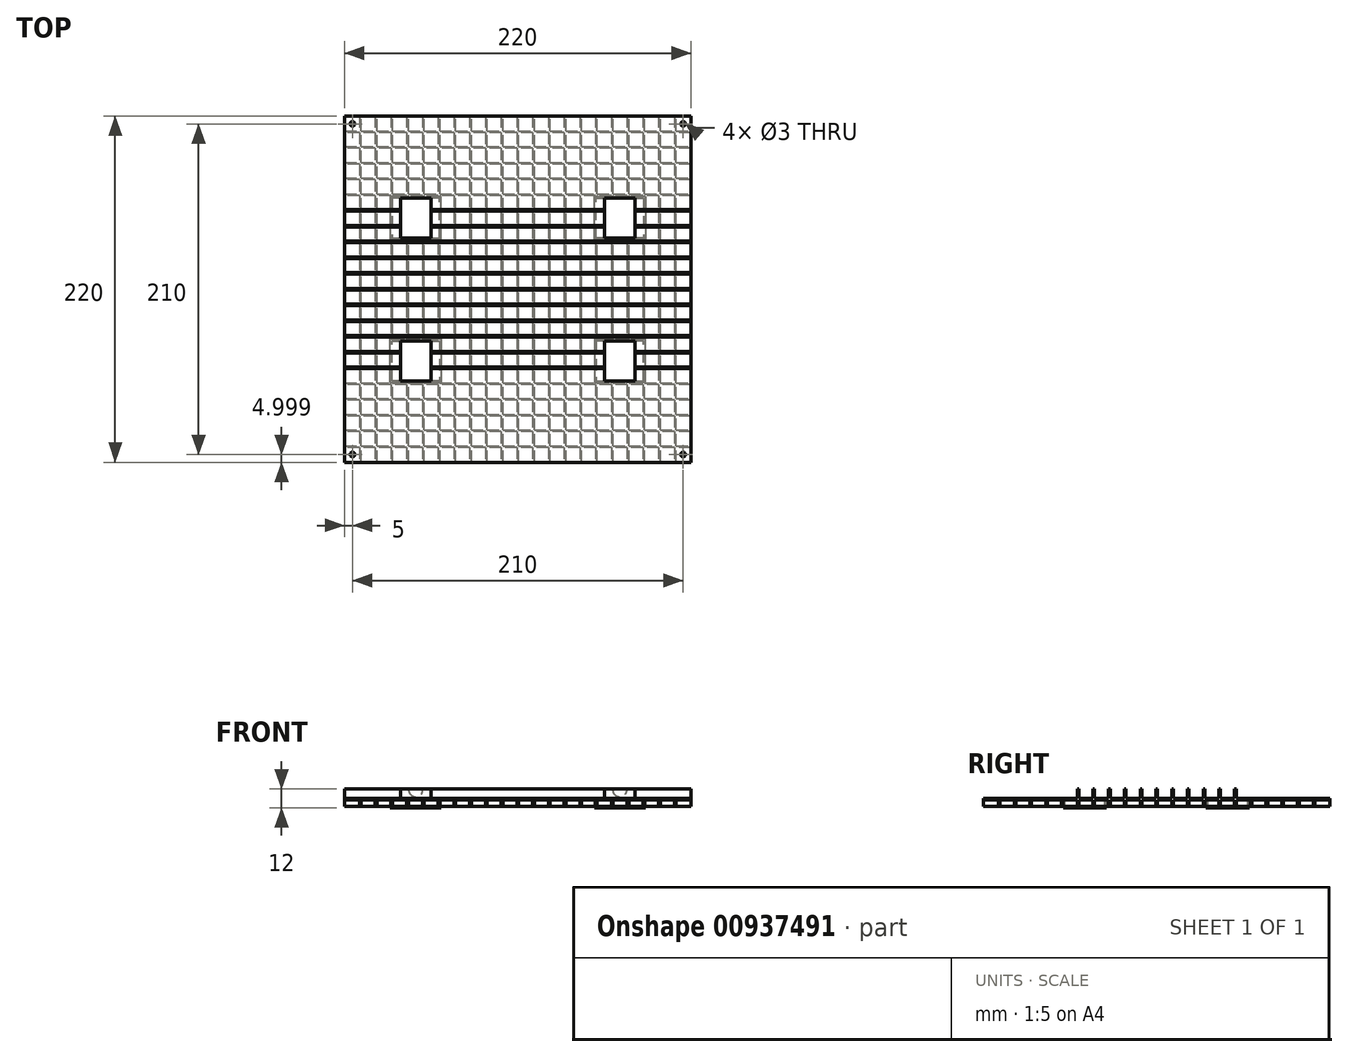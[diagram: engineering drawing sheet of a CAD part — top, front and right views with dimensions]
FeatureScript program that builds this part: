
annotation { "Feature Type Name" : "Feature", "Feature Type Description" : "" }
export const myFeature = defineFeature(function(context is Context, id is Id, definition is map)
    precondition{}
    {
        {
            var Q0;
            Q0=qCreatedBy(makeId("Top.planeOp"),FACE);
            var sketch = newSketch(context, id + "F0", { "sketchPlane" : qUnion([Q0])});
            skPoint(sketch, "E0", {"position": v(-105, 105.2) * mm});
            skPoint(sketch, "E1", {"position": v(105, 105.2) * mm});
            skPoint(sketch, "E2", {"position": v(105, -104.8) * mm});
            skPoint(sketch, "E3", {"position": v(-105, -104.8) * mm});
            skLineSegment(sketch, "E4.bottom", {"start": v(-110, 110.2) * mm, "end": v(110, 110.2) * mm});
            skLineSegment(sketch, "E4.top", {"start": v(-110, -109.8) * mm, "end": v(110, -109.8) * mm});
            skLineSegment(sketch, "E4.left", {"start": v(-110, 110.2) * mm, "end": v(-110, -109.8) * mm});
            skLineSegment(sketch, "E4.right", {"start": v(110, 110.2) * mm, "end": v(110, -109.8) * mm});
            skLineSegment(sketch, "E5", {"start": v(-105, 105.2) * mm, "end": v(-110, 105.2) * mm, "construction": true});
            skLineSegment(sketch, "E6", {"start": v(-105, 105.2) * mm, "end": v(-105, 110.2) * mm, "construction": true});
            skLineSegment(sketch, "E7", {"start": v(105, 105.2) * mm, "end": v(110, 105.2) * mm, "construction": true});
            skLineSegment(sketch, "E8", {"start": v(105, 105.2) * mm, "end": v(105, 110.2) * mm, "construction": true});
            skLineSegment(sketch, "E9", {"start": v(105, -104.8) * mm, "end": v(110, -104.8) * mm, "construction": true});
            skLineSegment(sketch, "E10", {"start": v(105, -104.8) * mm, "end": v(105, -109.8) * mm, "construction": true});
            skLineSegment(sketch, "E11", {"start": v(-105, -104.8) * mm, "end": v(-105, -109.8) * mm, "construction": true});
            skLineSegment(sketch, "E12", {"start": v(-105, -104.8) * mm, "end": v(-110, -104.8) * mm, "construction": true});
            skCircle(sketch, "E13", {"center": v(-105, 105.2) * mm, "radius": 1.5 * mm});
            skCircle(sketch, "E14", {"center": v(105, 105.2) * mm, "radius": 1.5 * mm});
            skCircle(sketch, "E15", {"center": v(105, -104.8) * mm, "radius": 1.5 * mm});
            skCircle(sketch, "E16", {"center": v(-105, -104.8) * mm, "radius": 1.5 * mm});
            skSolve(sketch);
        }
        {
            var Q0;
            Q0 = qSketchRegion(id + "F0", true);
            extrude(context, id + "F1", {"entities" : qUnion([Q0]), "oppositeDirection" : true, "depth" : 1 * mm, "offsetDistance" : 25 * mm});
        }
        {
            var Q0;
            Q0=makeQuery(id+"F1.opExtrude","CAP_FACE",FACE,{"disambiguationData":[OSD([sQuery(id+"F0.wireOp",EDGE,"E4.bottom"),sQuery(id+"F0.wireOp",EDGE,"E4.top"),sQuery(id+"F0.wireOp",EDGE,"E4.left"),sQuery(id+"F0.wireOp",EDGE,"E4.right"),sQuery(id+"F0.wireOp",EDGE,"b305908e-d21f-4fcc-82a1-d083eb46f08c.bottom"),sQuery(id+"F0.wireOp",EDGE,"b305908e-d21f-4fcc-82a1-d083eb46f08c.top"),sQuery(id+"F0.wireOp",EDGE,"b305908e-d21f-4fcc-82a1-d083eb46f08c.left"),sQuery(id+"F0.wireOp",EDGE,"b305908e-d21f-4fcc-82a1-d083eb46f08c.right"),sQuery(id+"F0.wireOp",EDGE,"ffc58e78-ab67-4520-8160-0caf265e7499.bottom"),sQuery(id+"F0.wireOp",EDGE,"ffc58e78-ab67-4520-8160-0caf265e7499.top"),sQuery(id+"F0.wireOp",EDGE,"ffc58e78-ab67-4520-8160-0caf265e7499.left"),sQuery(id+"F0.wireOp",EDGE,"ffc58e78-ab67-4520-8160-0caf265e7499.right"),sQuery(id+"F0.wireOp",EDGE,"050fb597-32a5-4862-9c33-4c7541ed5447.bottom"),sQuery(id+"F0.wireOp",EDGE,"050fb597-32a5-4862-9c33-4c7541ed5447.top"),sQuery(id+"F0.wireOp",EDGE,"050fb597-32a5-4862-9c33-4c7541ed5447.left"),sQuery(id+"F0.wireOp",EDGE,"050fb597-32a5-4862-9c33-4c7541ed5447.right"),sQuery(id+"F0.wireOp",EDGE,"796d922f-7def-4038-baac-653a5c7ec2cd.bottom"),sQuery(id+"F0.wireOp",EDGE,"796d922f-7def-4038-baac-653a5c7ec2cd.top"),sQuery(id+"F0.wireOp",EDGE,"796d922f-7def-4038-baac-653a5c7ec2cd.left"),sQuery(id+"F0.wireOp",EDGE,"796d922f-7def-4038-baac-653a5c7ec2cd.right"),sQuery(id+"F0.wireOp",EDGE,"E13"),sQuery(id+"F0.wireOp",EDGE,"E14"),sQuery(id+"F0.wireOp",EDGE,"E15"),sQuery(id+"F0.wireOp",EDGE,"E16")])],"isStart":false});
            var sketch = newSketch(context, id + "F2", { "sketchPlane" : qUnion([Q0])});
            skPoint(sketch, "E17.0", {"position": v(110, -110) * mm});
            skPoint(sketch, "E17.1", {"position": v(-110, -110) * mm});
            skPoint(sketch, "E17.2", {"position": v(110, 110) * mm});
            skPoint(sketch, "E17.3", {"position": v(-110, 110) * mm});
            skLineSegment(sketch, "E17.4", {"start": v(49.6, -32.6) * mm, "end": v(49.6, -58) * mm});
            skLineSegment(sketch, "E17.5", {"start": v(49.6, -58) * mm, "end": v(80, -58) * mm});
            skLineSegment(sketch, "E17.6", {"start": v(80, -58) * mm, "end": v(80, -32.6) * mm});
            skLineSegment(sketch, "E17.7", {"start": v(80, -32.6) * mm, "end": v(49.6, -32.6) * mm});
            skLineSegment(sketch, "E18", {"start": v(110, 110) * mm, "end": v(110, -110) * mm});
            skLineSegment(sketch, "E19", {"start": v(110, -110) * mm, "end": v(-110, -110) * mm});
            skLineSegment(sketch, "E20", {"start": v(-110, 110) * mm, "end": v(110, 110) * mm});
            skLineSegment(sketch, "E21", {"start": v(74.6, -58) * mm, "end": v(74.6, -32.6) * mm});
            skLineSegment(sketch, "E22", {"start": v(55, -58) * mm, "end": v(55, -32.6) * mm});
            skLineSegment(sketch, "E23.0", {"start": v(81, -31.6) * mm, "end": v(48.6, -31.6) * mm});
            skLineSegment(sketch, "E23.1", {"start": v(81, -59) * mm, "end": v(81, -31.6) * mm});
            skLineSegment(sketch, "E23.2", {"start": v(48.6, -59) * mm, "end": v(81, -59) * mm});
            skLineSegment(sketch, "E23.3", {"start": v(48.6, -31.6) * mm, "end": v(48.6, -59) * mm});
            skLineSegment(sketch, "E24", {"start": v(0, 0) * mm, "end": v(0, -10.79) * mm, "construction": true});
            skLineSegment(sketch, "E25", {"start": v(0, 0) * mm, "end": v(11.86, 0) * mm, "construction": true});
            skLineSegment(sketch, "E26.MirrorCS", {"start": v(-49.6, -58) * mm, "end": v(-80, -58) * mm});
            skLineSegment(sketch, "E27.MirrorCS", {"start": v(-80, -58) * mm, "end": v(-80, -32.6) * mm});
            skLineSegment(sketch, "E28.MirrorCS", {"start": v(-81, -59) * mm, "end": v(-81, -31.6) * mm});
            skLineSegment(sketch, "E29.MirrorCS", {"start": v(-55, -58) * mm, "end": v(-55, -32.6) * mm});
            skLineSegment(sketch, "E30.MirrorCS", {"start": v(-81, -31.6) * mm, "end": v(-48.6, -31.6) * mm});
            skLineSegment(sketch, "E31.MirrorCS", {"start": v(-48.6, -59) * mm, "end": v(-81, -59) * mm});
            skLineSegment(sketch, "E32.MirrorCS", {"start": v(-74.6, -58) * mm, "end": v(-74.6, -32.6) * mm});
            skLineSegment(sketch, "E33.MirrorCS", {"start": v(-80, -32.6) * mm, "end": v(-49.6, -32.6) * mm});
            skLineSegment(sketch, "E34.MirrorCS", {"start": v(-49.6, -32.6) * mm, "end": v(-49.6, -58) * mm});
            skLineSegment(sketch, "E35.MirrorCS", {"start": v(-48.6, -31.6) * mm, "end": v(-48.6, -59) * mm});
            skLineSegment(sketch, "E36.MirrorCS", {"start": v(-55, 58) * mm, "end": v(-55, 32.6) * mm});
            skLineSegment(sketch, "E37.MirrorCS", {"start": v(-80, 58) * mm, "end": v(-80, 32.6) * mm});
            skLineSegment(sketch, "E38.MirrorCS", {"start": v(48.6, 59) * mm, "end": v(81, 59) * mm});
            skLineSegment(sketch, "E39.MirrorCS", {"start": v(74.6, 58) * mm, "end": v(74.6, 32.6) * mm});
            skLineSegment(sketch, "E40.MirrorCS", {"start": v(49.6, 58) * mm, "end": v(80, 58) * mm});
            skLineSegment(sketch, "E41.MirrorCS", {"start": v(-80, 32.6) * mm, "end": v(-49.6, 32.6) * mm});
            skLineSegment(sketch, "E42.MirrorCS", {"start": v(80, 32.6) * mm, "end": v(49.6, 32.6) * mm});
            skLineSegment(sketch, "E43.MirrorCS", {"start": v(-81, 59) * mm, "end": v(-81, 31.6) * mm});
            skLineSegment(sketch, "E44.MirrorCS", {"start": v(49.6, 32.6) * mm, "end": v(49.6, 58) * mm});
            skLineSegment(sketch, "E45.MirrorCS", {"start": v(-48.6, 59) * mm, "end": v(-81, 59) * mm});
            skLineSegment(sketch, "E46.MirrorCS", {"start": v(-48.6, 31.6) * mm, "end": v(-48.6, 59) * mm});
            skLineSegment(sketch, "E47.MirrorCS", {"start": v(81, 31.6) * mm, "end": v(48.6, 31.6) * mm});
            skLineSegment(sketch, "E48.MirrorCS", {"start": v(-49.6, 32.6) * mm, "end": v(-49.6, 58) * mm});
            skLineSegment(sketch, "E49.MirrorCS", {"start": v(-49.6, 58) * mm, "end": v(-80, 58) * mm});
            skLineSegment(sketch, "E50.MirrorCS", {"start": v(81, 59) * mm, "end": v(81, 31.6) * mm});
            skLineSegment(sketch, "E51.MirrorCS", {"start": v(48.6, 31.6) * mm, "end": v(48.6, 59) * mm});
            skLineSegment(sketch, "E52.MirrorCS", {"start": v(55, 58) * mm, "end": v(55, 32.6) * mm});
            skLineSegment(sketch, "E53.MirrorCS", {"start": v(80, 58) * mm, "end": v(80, 32.6) * mm});
            skLineSegment(sketch, "E54.MirrorCS", {"start": v(-74.6, 58) * mm, "end": v(-74.6, 32.6) * mm});
            skLineSegment(sketch, "E55.MirrorCS", {"start": v(-81, 31.6) * mm, "end": v(-48.6, 31.6) * mm});
            skSolve(sketch);
        }
        {
            var Q0;
            Q0=qCreatedBy(makeId("Top.planeOp"),FACE);
            var sketch = newSketch(context, id + "F3", { "sketchPlane" : qUnion([Q0])});
            skLineSegment(sketch, "E56.0", {"start": v(-110, 110.2) * mm, "end": v(110, 110.2) * mm, "construction": true});
            skLineSegment(sketch, "E56.19", {"start": v(-110, -109.8) * mm, "end": v(110, -109.8) * mm, "construction": true});
            skCircle(sketch, "E56.20", {"center": v(-105, -104.8) * mm, "radius": 1.5 * mm, "construction": true});
            skCircle(sketch, "E56.21", {"center": v(105, -104.8) * mm, "radius": 1.5 * mm, "construction": true});
            skCircle(sketch, "E56.22", {"center": v(105, 105.2) * mm, "radius": 1.5 * mm, "construction": true});
            skCircle(sketch, "E56.23", {"center": v(-105, 105.2) * mm, "radius": 1.5 * mm, "construction": true});
            skLineSegment(sketch, "E57", {"start": v(-110, 100.7) * mm, "end": v(110, 100.7) * mm});
            skLineSegment(sketch, "E58", {"start": v(110, 99.7) * mm, "end": v(-110, 99.7) * mm});
            skLineSegment(sketch, "E59.0.1.0", {"start": v(-110, 90.7) * mm, "end": v(110, 90.7) * mm});
            skLineSegment(sketch, "E59.0.1.1", {"start": v(110, 89.7) * mm, "end": v(-110, 89.7) * mm});
            skLineSegment(sketch, "E59.0.2.0", {"start": v(-110, 80.7) * mm, "end": v(110, 80.7) * mm});
            skLineSegment(sketch, "E59.0.2.1", {"start": v(110, 79.7) * mm, "end": v(-110, 79.7) * mm});
            skLineSegment(sketch, "E59.0.3.0", {"start": v(-110, 70.7) * mm, "end": v(110, 70.7) * mm});
            skLineSegment(sketch, "E59.0.3.1", {"start": v(110, 69.7) * mm, "end": v(-110, 69.7) * mm});
            skLineSegment(sketch, "E59.0.4.0", {"start": v(-110, 60.7) * mm, "end": v(110, 60.7) * mm});
            skLineSegment(sketch, "E59.0.4.1", {"start": v(110, 59.7) * mm, "end": v(-110, 59.7) * mm});
            skLineSegment(sketch, "E59.0.5.0", {"start": v(-110, 50.7) * mm, "end": v(110, 50.7) * mm});
            skLineSegment(sketch, "E59.0.5.1", {"start": v(110, 49.7) * mm, "end": v(-110, 49.7) * mm});
            skLineSegment(sketch, "E59.0.6.0", {"start": v(-110, 40.7) * mm, "end": v(110, 40.7) * mm});
            skLineSegment(sketch, "E59.0.6.1", {"start": v(110, 39.7) * mm, "end": v(-110, 39.7) * mm});
            skLineSegment(sketch, "E59.0.7.0", {"start": v(-110, 30.7) * mm, "end": v(110, 30.7) * mm});
            skLineSegment(sketch, "E59.0.7.1", {"start": v(110, 29.7) * mm, "end": v(-110, 29.7) * mm});
            skLineSegment(sketch, "E59.0.8.0", {"start": v(-110, 20.7) * mm, "end": v(110, 20.7) * mm});
            skLineSegment(sketch, "E59.0.8.1", {"start": v(110, 19.7) * mm, "end": v(-110, 19.7) * mm});
            skLineSegment(sketch, "E59.0.9.0", {"start": v(-110, 10.7) * mm, "end": v(110, 10.7) * mm});
            skLineSegment(sketch, "E59.0.9.1", {"start": v(110, 9.7) * mm, "end": v(-110, 9.7) * mm});
            skLineSegment(sketch, "E59.0.10.0", {"start": v(-110, 0.7) * mm, "end": v(110, 0.7) * mm});
            skLineSegment(sketch, "E59.0.10.1", {"start": v(110, -0.3) * mm, "end": v(-110, -0.3) * mm});
            skLineSegment(sketch, "E59.0.11.0", {"start": v(-110, -9.3) * mm, "end": v(110, -9.3) * mm});
            skLineSegment(sketch, "E59.0.11.1", {"start": v(110, -10.3) * mm, "end": v(-110, -10.3) * mm});
            skLineSegment(sketch, "E59.0.12.0", {"start": v(-110, -19.3) * mm, "end": v(110, -19.3) * mm});
            skLineSegment(sketch, "E59.0.12.1", {"start": v(110, -20.3) * mm, "end": v(-110, -20.3) * mm});
            skLineSegment(sketch, "E59.0.13.0", {"start": v(-110, -29.3) * mm, "end": v(110, -29.3) * mm});
            skLineSegment(sketch, "E59.0.13.1", {"start": v(110, -30.3) * mm, "end": v(-110, -30.3) * mm});
            skLineSegment(sketch, "E59.0.14.0", {"start": v(-110, -39.3) * mm, "end": v(110, -39.3) * mm});
            skLineSegment(sketch, "E59.0.14.1", {"start": v(110, -40.3) * mm, "end": v(-110, -40.3) * mm});
            skLineSegment(sketch, "E59.0.15.0", {"start": v(-110, -49.3) * mm, "end": v(110, -49.3) * mm});
            skLineSegment(sketch, "E59.0.15.1", {"start": v(110, -50.3) * mm, "end": v(-110, -50.3) * mm});
            skLineSegment(sketch, "E59.0.16.0", {"start": v(-110, -59.3) * mm, "end": v(110, -59.3) * mm});
            skLineSegment(sketch, "E59.0.16.1", {"start": v(110, -60.3) * mm, "end": v(-110, -60.3) * mm});
            skLineSegment(sketch, "E59.0.17.0", {"start": v(-110, -69.3) * mm, "end": v(110, -69.3) * mm});
            skLineSegment(sketch, "E59.0.17.1", {"start": v(110, -70.3) * mm, "end": v(-110, -70.3) * mm});
            skLineSegment(sketch, "E59.0.18.0", {"start": v(-110, -79.3) * mm, "end": v(110, -79.3) * mm});
            skLineSegment(sketch, "E59.0.18.1", {"start": v(110, -80.3) * mm, "end": v(-110, -80.3) * mm});
            skLineSegment(sketch, "E59.0.19.0", {"start": v(-110, -89.3) * mm, "end": v(110, -89.3) * mm});
            skLineSegment(sketch, "E59.0.19.1", {"start": v(110, -90.3) * mm, "end": v(-110, -90.3) * mm});
            skLineSegment(sketch, "E59.0.20.0", {"start": v(-110, -99.3) * mm, "end": v(110, -99.3) * mm});
            skLineSegment(sketch, "E59.0.20.1", {"start": v(110, -100.3) * mm, "end": v(-110, -100.3) * mm});
            skLineSegment(sketch, "E59.direction1", {"start": v(-110, 99.7) * mm, "end": v(-85, 99.7) * mm, "construction": true});
            skLineSegment(sketch, "E60", {"start": v(-110, 100.7) * mm, "end": v(-110, 99.7) * mm});
            skLineSegment(sketch, "E61", {"start": v(110, -100.3) * mm, "end": v(110, -99.3) * mm});
            skLineSegment(sketch, "E62.trimOffspring", {"start": v(110, 99.7) * mm, "end": v(110, 100.7) * mm});
            skLineSegment(sketch, "E63.trimOffspring", {"start": v(110, 89.7) * mm, "end": v(110, 90.7) * mm});
            skLineSegment(sketch, "E64.trimOffspring", {"start": v(110, 79.7) * mm, "end": v(110, 80.7) * mm});
            skLineSegment(sketch, "E65.trimOffspring", {"start": v(110, 69.7) * mm, "end": v(110, 70.7) * mm});
            skLineSegment(sketch, "E66.trimOffspring", {"start": v(110, 59.7) * mm, "end": v(110, 60.7) * mm});
            skLineSegment(sketch, "E67.trimOffspring", {"start": v(110, 49.7) * mm, "end": v(110, 50.7) * mm});
            skLineSegment(sketch, "E68.trimOffspring", {"start": v(110, 39.7) * mm, "end": v(110, 40.7) * mm});
            skLineSegment(sketch, "E69.trimOffspring", {"start": v(110, 29.7) * mm, "end": v(110, 30.7) * mm});
            skLineSegment(sketch, "E70.trimOffspring", {"start": v(110, 19.7) * mm, "end": v(110, 20.7) * mm});
            skLineSegment(sketch, "E71.trimOffspring", {"start": v(110, 9.7) * mm, "end": v(110, 10.7) * mm});
            skLineSegment(sketch, "E72.trimOffspring", {"start": v(110, -0.3) * mm, "end": v(110, 0.7) * mm});
            skLineSegment(sketch, "E73.trimOffspring", {"start": v(110, -10.3) * mm, "end": v(110, -9.3) * mm});
            skLineSegment(sketch, "E74.trimOffspring", {"start": v(110, -20.3) * mm, "end": v(110, -19.3) * mm});
            skLineSegment(sketch, "E75.trimOffspring", {"start": v(110, -30.3) * mm, "end": v(110, -29.3) * mm});
            skLineSegment(sketch, "E76.trimOffspring", {"start": v(110, -40.3) * mm, "end": v(110, -39.3) * mm});
            skLineSegment(sketch, "E77.trimOffspring", {"start": v(110, -50.3) * mm, "end": v(110, -49.3) * mm});
            skLineSegment(sketch, "E78.trimOffspring", {"start": v(110, -60.3) * mm, "end": v(110, -59.3) * mm});
            skLineSegment(sketch, "E79.trimOffspring", {"start": v(110, -70.3) * mm, "end": v(110, -69.3) * mm});
            skLineSegment(sketch, "E80.trimOffspring", {"start": v(110, -80.3) * mm, "end": v(110, -79.3) * mm});
            skLineSegment(sketch, "E81.trimOffspring", {"start": v(110, -90.3) * mm, "end": v(110, -89.3) * mm});
            skLineSegment(sketch, "E82.trimOffspring", {"start": v(-110, -99.3) * mm, "end": v(-110, -100.3) * mm});
            skLineSegment(sketch, "E83.trimOffspring", {"start": v(-110, -89.3) * mm, "end": v(-110, -90.3) * mm});
            skLineSegment(sketch, "E84.trimOffspring", {"start": v(-110, -79.3) * mm, "end": v(-110, -80.3) * mm});
            skLineSegment(sketch, "E85.trimOffspring", {"start": v(-110, -69.3) * mm, "end": v(-110, -70.3) * mm});
            skLineSegment(sketch, "E86.trimOffspring", {"start": v(-110, -59.3) * mm, "end": v(-110, -60.3) * mm});
            skLineSegment(sketch, "E87.trimOffspring", {"start": v(-110, -49.3) * mm, "end": v(-110, -50.3) * mm});
            skLineSegment(sketch, "E88.trimOffspring", {"start": v(-110, -39.3) * mm, "end": v(-110, -40.3) * mm});
            skLineSegment(sketch, "E89.trimOffspring", {"start": v(-110, -29.3) * mm, "end": v(-110, -30.3) * mm});
            skLineSegment(sketch, "E90.trimOffspring", {"start": v(-110, -19.3) * mm, "end": v(-110, -20.3) * mm});
            skLineSegment(sketch, "E91.trimOffspring", {"start": v(-110, -9.3) * mm, "end": v(-110, -10.3) * mm});
            skLineSegment(sketch, "E92.trimOffspring", {"start": v(-110, 0.7) * mm, "end": v(-110, -0.3) * mm});
            skLineSegment(sketch, "E93.trimOffspring", {"start": v(-110, 10.7) * mm, "end": v(-110, 9.7) * mm});
            skLineSegment(sketch, "E94.trimOffspring", {"start": v(-110, 20.7) * mm, "end": v(-110, 19.7) * mm});
            skLineSegment(sketch, "E95.trimOffspring", {"start": v(-110, 30.7) * mm, "end": v(-110, 29.7) * mm});
            skLineSegment(sketch, "E96.trimOffspring", {"start": v(-110, 40.7) * mm, "end": v(-110, 39.7) * mm});
            skLineSegment(sketch, "E97.trimOffspring", {"start": v(-110, 50.7) * mm, "end": v(-110, 49.7) * mm});
            skLineSegment(sketch, "E98.trimOffspring", {"start": v(-110, 60.7) * mm, "end": v(-110, 59.7) * mm});
            skLineSegment(sketch, "E99.trimOffspring", {"start": v(-110, 70.7) * mm, "end": v(-110, 69.7) * mm});
            skLineSegment(sketch, "E100.trimOffspring", {"start": v(-110, 80.7) * mm, "end": v(-110, 79.7) * mm});
            skLineSegment(sketch, "E101.trimOffspring", {"start": v(-110, 90.7) * mm, "end": v(-110, 89.7) * mm});
            skLineSegment(sketch, "E102.0", {"start": v(70, -29.3) * mm, "end": v(70, -30.3) * mm});
            skLineSegment(sketch, "E102.1", {"start": v(101, -50.3) * mm, "end": v(101, -49.3) * mm});
            skLineSegment(sketch, "E103.0", {"start": v(101, 29.7) * mm, "end": v(101, 30.7) * mm});
            skLineSegment(sketch, "E103.1", {"start": v(70, 29.7) * mm, "end": v(70, 30.7) * mm});
            skLineSegment(sketch, "E103.2", {"start": v(-70, 29.7) * mm, "end": v(-70, 30.7) * mm});
            skLineSegment(sketch, "E103.3", {"start": v(-101, 29.7) * mm, "end": v(-101, 30.7) * mm});
            skLineSegment(sketch, "E103.4", {"start": v(-101, -29.3) * mm, "end": v(-101, -30.3) * mm});
            skLineSegment(sketch, "E103.5", {"start": v(-70, -29.3) * mm, "end": v(-70, -30.3) * mm});
            skLineSegment(sketch, "E104.trimOffspring", {"start": v(101, 49.7) * mm, "end": v(101, 50.7) * mm});
            skLineSegment(sketch, "E105.trimOffspring", {"start": v(101, 39.7) * mm, "end": v(101, 40.7) * mm});
            skLineSegment(sketch, "E106.trimOffspring", {"start": v(70, 39.7) * mm, "end": v(70, 40.7) * mm});
            skLineSegment(sketch, "E107.trimOffspring", {"start": v(70, 49.7) * mm, "end": v(70, 50.7) * mm});
            skLineSegment(sketch, "E108.trimOffspring", {"start": v(-70, 49.7) * mm, "end": v(-70, 50.7) * mm});
            skLineSegment(sketch, "E109.trimOffspring", {"start": v(-70, 39.7) * mm, "end": v(-70, 40.7) * mm});
            skLineSegment(sketch, "E110.trimOffspring", {"start": v(-101, 39.7) * mm, "end": v(-101, 40.7) * mm});
            skLineSegment(sketch, "E111.trimOffspring", {"start": v(-101, 49.7) * mm, "end": v(-101, 50.7) * mm});
            skLineSegment(sketch, "E112.trimOffspring", {"start": v(-101, -39.3) * mm, "end": v(-101, -40.3) * mm});
            skLineSegment(sketch, "E113.trimOffspring", {"start": v(-101, -49.3) * mm, "end": v(-101, -50.3) * mm});
            skLineSegment(sketch, "E114.trimOffspring", {"start": v(-70, -49.3) * mm, "end": v(-70, -50.3) * mm});
            skLineSegment(sketch, "E115.trimOffspring", {"start": v(-70, -39.3) * mm, "end": v(-70, -40.3) * mm});
            skLineSegment(sketch, "E116.trimOffspring", {"start": v(101, -30.3) * mm, "end": v(101, -29.3) * mm});
            skLineSegment(sketch, "E117.trimOffspring", {"start": v(70, -39.3) * mm, "end": v(70, -40.3) * mm});
            skLineSegment(sketch, "E118.trimOffspring", {"start": v(70, -49.3) * mm, "end": v(70, -50.3) * mm});
            skLineSegment(sketch, "E119", {"start": v(101, -39.3) * mm, "end": v(101, -40.3) * mm});
            skPoint(sketch, "E120.0", {"position": v(-110, 110.2) * mm});
            skSolve(sketch);
        }
        {
            var Q0;
            Q0=makeQuery(id+"F3.imprint","IMPRINT",FACE,{"disambiguationData":[TD([[makeQuery(id+"F3.imprint","IMPRINT",EDGE,{"derivedFrom":sQuery(id+"F3.wireOp",EDGE,"E59.0.18.0")}),-1.0]])]});
            var Q1;
            Q1=makeQuery(id+"F3.imprint","IMPRINT",FACE,{"disambiguationData":[TD([[makeQuery(id+"F3.imprint","IMPRINT",EDGE,{"derivedFrom":sQuery(id+"F3.wireOp",EDGE,"E59.0.17.0")}),-1.0]])]});
            var Q2;
            Q2=makeQuery(id+"F3.imprint","IMPRINT",FACE,{"disambiguationData":[TD([[makeQuery(id+"F3.imprint","IMPRINT",EDGE,{"derivedFrom":sQuery(id+"F3.wireOp",EDGE,"E59.0.16.0")}),-1.0]])]});
            var Q3;
            Q3=makeQuery(id+"F3.imprint","IMPRINT",FACE,{"disambiguationData":[TD([[makeQuery(id+"F3.imprint","IMPRINT",EDGE,{"derivedFrom":sQuery(id+"F3.wireOp",EDGE,"E59.0.11.0")}),-1.0]])]});
            var Q4;
            Q4=makeQuery(id+"F3.imprint","IMPRINT",FACE,{"disambiguationData":[TD([[makeQuery(id+"F3.imprint","IMPRINT",EDGE,{"derivedFrom":sQuery(id+"F3.wireOp",EDGE,"E59.0.10.0")}),-1.0]])]});
            var Q5;
            Q5=makeQuery(id+"F3.imprint","IMPRINT",FACE,{"disambiguationData":[TD([[makeQuery(id+"F3.imprint","IMPRINT",EDGE,{"derivedFrom":sQuery(id+"F3.wireOp",EDGE,"E59.0.9.0")}),-1.0]])]});
            var Q6;
            Q6=makeQuery(id+"F3.imprint","IMPRINT",FACE,{"disambiguationData":[TD([[makeQuery(id+"F3.imprint","IMPRINT",EDGE,{"derivedFrom":sQuery(id+"F3.wireOp",EDGE,"E59.0.4.0")}),-1.0]])]});
            var Q7;
            Q7=makeQuery(id+"F3.imprint","IMPRINT",FACE,{"disambiguationData":[TD([[makeQuery(id+"F3.imprint","IMPRINT",EDGE,{"derivedFrom":sQuery(id+"F3.wireOp",EDGE,"E59.0.3.0")}),-1.0]])]});
            var Q8;
            Q8=makeQuery(id+"F3.imprint","IMPRINT",FACE,{"disambiguationData":[TD([[makeQuery(id+"F3.imprint","IMPRINT",EDGE,{"derivedFrom":sQuery(id+"F3.wireOp",EDGE,"E59.0.2.0")}),-1.0]])]});
            var Q9;
            {var subQ1=sQuery(id+"F2.wireOp",EDGE,"E17.4");Q9=makeQuery(id+"F2.imprint","IMPRINT",FACE,{"disambiguationData":[TD([[makeQuery(id+"F2.imprint","IMPRINT",EDGE,{"derivedFrom":subQ1}),-1.0]])]});}
            var Q10;
            Q10=makeQuery(id+"F3.imprint","IMPRINT",FACE,{"disambiguationData":[TD([[makeQuery(id+"F3.imprint","IMPRINT",EDGE,{"derivedFrom":sQuery(id+"F3.wireOp",EDGE,"E57")}),-1.0]])]});
            var Q11;
            Q11=makeQuery(id+"F3.imprint","IMPRINT",FACE,{"disambiguationData":[TD([[makeQuery(id+"F3.imprint","IMPRINT",EDGE,{"derivedFrom":sQuery(id+"F3.wireOp",EDGE,"E59.0.1.0")}),-1.0]])]});
            var Q12;
            {var subQ0=sQuery(id+"F3.wireOp",EDGE,"E97.trimOffspring");Q12=makeQuery(id+"F3.imprint","IMPRINT",FACE,{"disambiguationData":[TD([[makeQuery(id+"F3.imprint","IMPRINT",EDGE,{"derivedFrom":subQ0}),1.0]])]});}
            var Q13;
            {var subQ0=sQuery(id+"F3.wireOp",EDGE,"E107.trimOffspring");Q13=makeQuery(id+"F3.imprint","IMPRINT",FACE,{"disambiguationData":[TD([[makeQuery(id+"F3.imprint","IMPRINT",EDGE,{"derivedFrom":subQ0}),1.0]])]});}
            var Q14;
            {var subQ0=sQuery(id+"F3.wireOp",EDGE,"E106.trimOffspring");Q14=makeQuery(id+"F3.imprint","IMPRINT",FACE,{"disambiguationData":[TD([[makeQuery(id+"F3.imprint","IMPRINT",EDGE,{"derivedFrom":subQ0}),1.0]])]});}
            var Q15;
            {var subQ0=sQuery(id+"F3.wireOp",EDGE,"E96.trimOffspring");Q15=makeQuery(id+"F3.imprint","IMPRINT",FACE,{"disambiguationData":[TD([[makeQuery(id+"F3.imprint","IMPRINT",EDGE,{"derivedFrom":subQ0}),1.0]])]});}
            var Q16;
            {var subQ0=sQuery(id+"F3.wireOp",EDGE,"E95.trimOffspring");Q16=makeQuery(id+"F3.imprint","IMPRINT",FACE,{"disambiguationData":[TD([[makeQuery(id+"F3.imprint","IMPRINT",EDGE,{"derivedFrom":subQ0}),1.0]])]});}
            var Q17;
            {var subQ0=sQuery(id+"F3.wireOp",EDGE,"E103.1");Q17=makeQuery(id+"F3.imprint","IMPRINT",FACE,{"disambiguationData":[TD([[makeQuery(id+"F3.imprint","IMPRINT",EDGE,{"derivedFrom":subQ0}),1.0]])]});}
            var Q18;
            Q18=makeQuery(id+"F3.imprint","IMPRINT",FACE,{"disambiguationData":[TD([[makeQuery(id+"F3.imprint","IMPRINT",EDGE,{"derivedFrom":sQuery(id+"F3.wireOp",EDGE,"E59.0.8.0")}),-1.0]])]});
            var Q19;
            {var subQ0=sQuery(id+"F3.wireOp",EDGE,"E104.trimOffspring");Q19=makeQuery(id+"F3.imprint","IMPRINT",FACE,{"disambiguationData":[TD([[makeQuery(id+"F3.imprint","IMPRINT",EDGE,{"derivedFrom":subQ0}),1.0]])]});}
            var Q20;
            {var subQ0=sQuery(id+"F3.wireOp",EDGE,"E67.trimOffspring");Q20=makeQuery(id+"F3.imprint","IMPRINT",FACE,{"disambiguationData":[TD([[makeQuery(id+"F3.imprint","IMPRINT",EDGE,{"derivedFrom":subQ0}),1.0]])]});}
            var Q21;
            {var subQ0=sQuery(id+"F3.wireOp",EDGE,"E105.trimOffspring");Q21=makeQuery(id+"F3.imprint","IMPRINT",FACE,{"disambiguationData":[TD([[makeQuery(id+"F3.imprint","IMPRINT",EDGE,{"derivedFrom":subQ0}),1.0]])]});}
            var Q22;
            {var subQ0=sQuery(id+"F3.wireOp",EDGE,"E68.trimOffspring");Q22=makeQuery(id+"F3.imprint","IMPRINT",FACE,{"disambiguationData":[TD([[makeQuery(id+"F3.imprint","IMPRINT",EDGE,{"derivedFrom":subQ0}),1.0]])]});}
            var Q23;
            {var subQ0=sQuery(id+"F3.wireOp",EDGE,"E103.0");Q23=makeQuery(id+"F3.imprint","IMPRINT",FACE,{"disambiguationData":[TD([[makeQuery(id+"F3.imprint","IMPRINT",EDGE,{"derivedFrom":subQ0}),1.0]])]});}
            var Q24;
            {var subQ0=sQuery(id+"F3.wireOp",EDGE,"E69.trimOffspring");Q24=makeQuery(id+"F3.imprint","IMPRINT",FACE,{"disambiguationData":[TD([[makeQuery(id+"F3.imprint","IMPRINT",EDGE,{"derivedFrom":subQ0}),1.0]])]});}
            var Q25;
            {var subQ0=sQuery(id+"F3.wireOp",EDGE,"E103.2");Q25=makeQuery(id+"F3.imprint","IMPRINT",FACE,{"disambiguationData":[TD([[makeQuery(id+"F3.imprint","IMPRINT",EDGE,{"derivedFrom":subQ0}),1.0]])]});}
            var Q26;
            {var subQ0=sQuery(id+"F3.wireOp",EDGE,"E109.trimOffspring");Q26=makeQuery(id+"F3.imprint","IMPRINT",FACE,{"disambiguationData":[TD([[makeQuery(id+"F3.imprint","IMPRINT",EDGE,{"derivedFrom":subQ0}),1.0]])]});}
            var Q27;
            {var subQ0=sQuery(id+"F3.wireOp",EDGE,"E108.trimOffspring");Q27=makeQuery(id+"F3.imprint","IMPRINT",FACE,{"disambiguationData":[TD([[makeQuery(id+"F3.imprint","IMPRINT",EDGE,{"derivedFrom":subQ0}),1.0]])]});}
            var Q28;
            {var subQ0=sQuery(id+"F3.wireOp",EDGE,"E89.trimOffspring");Q28=makeQuery(id+"F3.imprint","IMPRINT",FACE,{"disambiguationData":[TD([[makeQuery(id+"F3.imprint","IMPRINT",EDGE,{"derivedFrom":subQ0}),1.0]])]});}
            var Q29;
            {var subQ0=sQuery(id+"F3.wireOp",EDGE,"E103.4");Q29=makeQuery(id+"F3.imprint","IMPRINT",FACE,{"disambiguationData":[TD([[makeQuery(id+"F3.imprint","IMPRINT",EDGE,{"derivedFrom":subQ0}),1.0]])]});}
            var Q30;
            {var subQ0=sQuery(id+"F3.wireOp",EDGE,"E88.trimOffspring");Q30=makeQuery(id+"F3.imprint","IMPRINT",FACE,{"disambiguationData":[TD([[makeQuery(id+"F3.imprint","IMPRINT",EDGE,{"derivedFrom":subQ0}),1.0]])]});}
            var Q31;
            {var subQ0=sQuery(id+"F3.wireOp",EDGE,"E112.trimOffspring");Q31=makeQuery(id+"F3.imprint","IMPRINT",FACE,{"disambiguationData":[TD([[makeQuery(id+"F3.imprint","IMPRINT",EDGE,{"derivedFrom":subQ0}),1.0]])]});}
            var Q32;
            Q32=makeQuery(id+"F3.imprint","IMPRINT",FACE,{"disambiguationData":[TD([[makeQuery(id+"F3.imprint","IMPRINT",EDGE,{"derivedFrom":sQuery(id+"F3.wireOp",EDGE,"E59.0.12.0")}),-1.0]])]});
            var Q33;
            {var subQ0=sQuery(id+"F3.wireOp",EDGE,"E87.trimOffspring");Q33=makeQuery(id+"F3.imprint","IMPRINT",FACE,{"disambiguationData":[TD([[makeQuery(id+"F3.imprint","IMPRINT",EDGE,{"derivedFrom":subQ0}),1.0]])]});}
            var Q34;
            {var subQ0=sQuery(id+"F3.wireOp",EDGE,"E113.trimOffspring");Q34=makeQuery(id+"F3.imprint","IMPRINT",FACE,{"disambiguationData":[TD([[makeQuery(id+"F3.imprint","IMPRINT",EDGE,{"derivedFrom":subQ0}),1.0]])]});}
            var Q35;
            {var subQ0=sQuery(id+"F3.wireOp",EDGE,"E114.trimOffspring");Q35=makeQuery(id+"F3.imprint","IMPRINT",FACE,{"disambiguationData":[TD([[makeQuery(id+"F3.imprint","IMPRINT",EDGE,{"derivedFrom":subQ0}),1.0]])]});}
            var Q36;
            {var subQ0=sQuery(id+"F3.wireOp",EDGE,"E115.trimOffspring");Q36=makeQuery(id+"F3.imprint","IMPRINT",FACE,{"disambiguationData":[TD([[makeQuery(id+"F3.imprint","IMPRINT",EDGE,{"derivedFrom":subQ0}),1.0]])]});}
            var Q37;
            {var subQ0=sQuery(id+"F3.wireOp",EDGE,"E102.0");Q37=makeQuery(id+"F3.imprint","IMPRINT",FACE,{"disambiguationData":[TD([[makeQuery(id+"F3.imprint","IMPRINT",EDGE,{"derivedFrom":subQ0}),-1.0]])]});}
            var Q38;
            {var subQ0=sQuery(id+"F3.wireOp",EDGE,"E77.trimOffspring");Q38=makeQuery(id+"F3.imprint","IMPRINT",FACE,{"disambiguationData":[TD([[makeQuery(id+"F3.imprint","IMPRINT",EDGE,{"derivedFrom":subQ0}),1.0]])]});}
            var Q39;
            {var subQ0=sQuery(id+"F3.wireOp",EDGE,"E76.trimOffspring");Q39=makeQuery(id+"F3.imprint","IMPRINT",FACE,{"disambiguationData":[TD([[makeQuery(id+"F3.imprint","IMPRINT",EDGE,{"derivedFrom":subQ0}),1.0]])]});}
            var Q40;
            {var subQ0=sQuery(id+"F3.wireOp",EDGE,"E75.trimOffspring");Q40=makeQuery(id+"F3.imprint","IMPRINT",FACE,{"disambiguationData":[TD([[makeQuery(id+"F3.imprint","IMPRINT",EDGE,{"derivedFrom":subQ0}),1.0]])]});}
            var Q41;
            {var subQ0=sQuery(id+"F3.wireOp",EDGE,"E102.0");Q41=makeQuery(id+"F3.imprint","IMPRINT",FACE,{"disambiguationData":[TD([[makeQuery(id+"F3.imprint","IMPRINT",EDGE,{"derivedFrom":subQ0}),1.0]])]});}
            var Q42;
            {var subQ0=sQuery(id+"F3.wireOp",EDGE,"E117.trimOffspring");Q42=makeQuery(id+"F3.imprint","IMPRINT",FACE,{"disambiguationData":[TD([[makeQuery(id+"F3.imprint","IMPRINT",EDGE,{"derivedFrom":subQ0}),1.0]])]});}
            var Q43;
            {var subQ0=sQuery(id+"F3.wireOp",EDGE,"E102.1");Q43=makeQuery(id+"F3.imprint","IMPRINT",FACE,{"disambiguationData":[TD([[makeQuery(id+"F3.imprint","IMPRINT",EDGE,{"derivedFrom":subQ0}),1.0]])]});}
            var Q44;
            Q44=makeQuery(id+"F3.imprint","IMPRINT",FACE,{"disambiguationData":[TD([[makeQuery(id+"F3.imprint","IMPRINT",EDGE,{"derivedFrom":sQuery(id+"F3.wireOp",EDGE,"E59.0.19.0")}),-1.0]])]});
            var Q45;
            Q45=makeQuery(id+"F3.imprint","IMPRINT",FACE,{"disambiguationData":[TD([[makeQuery(id+"F3.imprint","IMPRINT",EDGE,{"derivedFrom":sQuery(id+"F3.wireOp",EDGE,"E59.0.20.0")}),-1.0]])]});
            var Q46;
            Q46=makeQuery(id+"F2.imprint","IMPRINT",FACE,{"disambiguationData":[TD([[makeQuery(id+"F2.imprint","IMPRINT",EDGE,{"derivedFrom":sQuery(id+"F2.wireOp",EDGE,"E38.MirrorCS")}),-1.0]])]});
            var Q47;
            {var subQ0=sQuery(id+"F2.wireOp",EDGE,"E37.MirrorCS");Q47=makeQuery(id+"F2.imprint","IMPRINT",FACE,{"disambiguationData":[TD([[makeQuery(id+"F2.imprint","IMPRINT",EDGE,{"derivedFrom":subQ0}),-1.0]])]});}
            var Q48;
            {var subQ5=sQuery(id+"F2.wireOp",EDGE,"E27.MirrorCS");Q48=makeQuery(id+"F2.imprint","IMPRINT",FACE,{"disambiguationData":[TD([[makeQuery(id+"F2.imprint","IMPRINT",EDGE,{"derivedFrom":subQ5}),1.0]])]});}
            extrude(context, id + "F4", {"entities" : qUnion([Q0, Q1, Q2, Q3, Q4, Q5, Q6, Q7, Q8, Q9, Q10, Q11, Q12, Q13, Q14, Q15, Q16, Q17, Q18, Q19, Q20, Q21, Q22, Q23, Q24, Q25, Q26, Q27, Q28, Q29, Q30, Q31, Q32, Q33, Q34, Q35, Q36, Q37, Q38, Q39, Q40, Q41, Q42, Q43, Q44, Q45, Q46, Q47, Q48]), "operationType" : NewBodyOperationType.ADD, "oppositeDirection" : true, "depth" : 5 * mm, "offsetDistance" : 25 * mm});
        }
        {
            var Q0;
            Q0=makeQuery(id+"F3.imprint","IMPRINT",FACE,{"disambiguationData":[TD([[makeQuery(id+"F3.imprint","IMPRINT",EDGE,{"derivedFrom":sQuery(id+"F3.wireOp",EDGE,"E59.0.5.0")}),-1.0]])]});
            var Q1;
            Q1=makeQuery(id+"F3.imprint","IMPRINT",FACE,{"disambiguationData":[TD([[makeQuery(id+"F3.imprint","IMPRINT",EDGE,{"derivedFrom":sQuery(id+"F3.wireOp",EDGE,"E59.0.6.0")}),-1.0]])]});
            var Q2;
            Q2=makeQuery(id+"F3.imprint","IMPRINT",FACE,{"disambiguationData":[TD([[makeQuery(id+"F3.imprint","IMPRINT",EDGE,{"derivedFrom":sQuery(id+"F3.wireOp",EDGE,"E59.0.7.0")}),-1.0]])]});
            var Q3;
            Q3=makeQuery(id+"F3.imprint","IMPRINT",FACE,{"disambiguationData":[TD([[makeQuery(id+"F3.imprint","IMPRINT",EDGE,{"derivedFrom":sQuery(id+"F3.wireOp",EDGE,"E59.0.8.0")}),-1.0]])]});
            var Q4;
            Q4=makeQuery(id+"F3.imprint","IMPRINT",FACE,{"disambiguationData":[TD([[makeQuery(id+"F3.imprint","IMPRINT",EDGE,{"derivedFrom":sQuery(id+"F3.wireOp",EDGE,"E59.0.9.0")}),-1.0]])]});
            var Q5;
            Q5=makeQuery(id+"F3.imprint","IMPRINT",FACE,{"disambiguationData":[TD([[makeQuery(id+"F3.imprint","IMPRINT",EDGE,{"derivedFrom":sQuery(id+"F3.wireOp",EDGE,"E59.0.10.0")}),-1.0]])]});
            var Q6;
            Q6=makeQuery(id+"F3.imprint","IMPRINT",FACE,{"disambiguationData":[TD([[makeQuery(id+"F3.imprint","IMPRINT",EDGE,{"derivedFrom":sQuery(id+"F3.wireOp",EDGE,"E59.0.11.0")}),-1.0]])]});
            var Q7;
            Q7=makeQuery(id+"F3.imprint","IMPRINT",FACE,{"disambiguationData":[TD([[makeQuery(id+"F3.imprint","IMPRINT",EDGE,{"derivedFrom":sQuery(id+"F3.wireOp",EDGE,"E59.0.12.0")}),-1.0]])]});
            var Q8;
            Q8=makeQuery(id+"F3.imprint","IMPRINT",FACE,{"disambiguationData":[TD([[makeQuery(id+"F3.imprint","IMPRINT",EDGE,{"derivedFrom":sQuery(id+"F3.wireOp",EDGE,"E59.0.13.0")}),-1.0]])]});
            var Q9;
            Q9=makeQuery(id+"F3.imprint","IMPRINT",FACE,{"disambiguationData":[TD([[makeQuery(id+"F3.imprint","IMPRINT",EDGE,{"derivedFrom":sQuery(id+"F3.wireOp",EDGE,"E59.0.14.0")}),-1.0]])]});
            var Q10;
            Q10=makeQuery(id+"F3.imprint","IMPRINT",FACE,{"disambiguationData":[TD([[makeQuery(id+"F3.imprint","IMPRINT",EDGE,{"derivedFrom":sQuery(id+"F3.wireOp",EDGE,"E59.0.15.0")}),-1.0]])]});
            extrude(context, id + "F5", {"entities" : qUnion([Q0, Q1, Q2, Q3, Q4, Q5, Q6, Q7, Q8, Q9, Q10]), "operationType" : NewBodyOperationType.ADD, "depth" : 6 * mm, "offsetDistance" : 25 * mm});
        }
        {
            var Q0;
            Q0=qCreatedBy(makeId("Top.planeOp"),FACE);
            var sketch = newSketch(context, id + "F6", { "sketchPlane" : qUnion([Q0])});
            skLineSegment(sketch, "E121.2", {"start": v(90, 52.2) * mm, "end": v(90, 20.2) * mm, "construction": true});
            skLineSegment(sketch, "E121.3", {"start": v(80, 52.2) * mm, "end": v(90, 52.2) * mm, "construction": true});
            skLineSegment(sketch, "E121.4", {"start": v(80, 52.2) * mm, "end": v(80, 20.2) * mm, "construction": true});
            skLineSegment(sketch, "E121.5", {"start": v(80, 20.2) * mm, "end": v(90, 20.2) * mm, "construction": true});
            skLineSegment(sketch, "E121.6", {"start": v(80, -51.8) * mm, "end": v(90, -51.8) * mm, "construction": true});
            skLineSegment(sketch, "E121.7", {"start": v(80, -19.8) * mm, "end": v(80, -51.8) * mm, "construction": true});
            skLineSegment(sketch, "E121.8", {"start": v(80, -19.8) * mm, "end": v(90, -19.8) * mm, "construction": true});
            skLineSegment(sketch, "E121.9", {"start": v(90, -19.8) * mm, "end": v(90, -51.8) * mm, "construction": true});
            skLineSegment(sketch, "E121.10", {"start": v(-90, -51.8) * mm, "end": v(-80, -51.8) * mm, "construction": true});
            skLineSegment(sketch, "E121.11", {"start": v(-90, -19.8) * mm, "end": v(-90, -51.8) * mm, "construction": true});
            skLineSegment(sketch, "E121.12", {"start": v(-90, -19.8) * mm, "end": v(-80, -19.8) * mm, "construction": true});
            skLineSegment(sketch, "E121.13", {"start": v(-80, -19.8) * mm, "end": v(-80, -51.8) * mm, "construction": true});
            skLineSegment(sketch, "E121.14", {"start": v(-90, 20.2) * mm, "end": v(-80, 20.2) * mm, "construction": true});
            skLineSegment(sketch, "E121.15", {"start": v(-90, 52.2) * mm, "end": v(-90, 20.2) * mm, "construction": true});
            skLineSegment(sketch, "E121.16", {"start": v(-90, 52.2) * mm, "end": v(-80, 52.2) * mm, "construction": true});
            skLineSegment(sketch, "E121.17", {"start": v(-80, 52.2) * mm, "end": v(-80, 20.2) * mm, "construction": true});
            skLineSegment(sketch, "E122", {"start": v(-100.5, 110.2) * mm, "end": v(-100.5, -109.8) * mm});
            skLineSegment(sketch, "E123", {"start": v(-100.5, -109.8) * mm, "end": v(-99.5, -109.8) * mm});
            skLineSegment(sketch, "E124", {"start": v(-99.5, -109.8) * mm, "end": v(-99.5, 110.2) * mm});
            skLineSegment(sketch, "E125", {"start": v(-99.5, 110.2) * mm, "end": v(-100.5, 110.2) * mm});
            skLineSegment(sketch, "E126.1.0.0", {"start": v(-90.5, 110.2) * mm, "end": v(-90.5, -109.8) * mm});
            skLineSegment(sketch, "E126.1.0.1", {"start": v(-89.5, -109.8) * mm, "end": v(-89.5, 110.2) * mm});
            skLineSegment(sketch, "E126.1.0.2", {"start": v(-90.5, -109.8) * mm, "end": v(-89.5, -109.8) * mm});
            skLineSegment(sketch, "E126.1.0.3", {"start": v(-89.5, 110.2) * mm, "end": v(-90.5, 110.2) * mm});
            skLineSegment(sketch, "E126.2.0.0", {"start": v(-80.5, 110.2) * mm, "end": v(-80.5, -109.8) * mm});
            skLineSegment(sketch, "E126.2.0.1", {"start": v(-79.5, -109.8) * mm, "end": v(-79.5, 110.2) * mm});
            skLineSegment(sketch, "E126.2.0.2", {"start": v(-80.5, -109.8) * mm, "end": v(-79.5, -109.8) * mm});
            skLineSegment(sketch, "E126.2.0.3", {"start": v(-79.5, 110.2) * mm, "end": v(-80.5, 110.2) * mm});
            skLineSegment(sketch, "E126.3.0.0", {"start": v(-70.5, 110.2) * mm, "end": v(-70.5, -109.8) * mm});
            skLineSegment(sketch, "E126.3.0.1", {"start": v(-69.5, -109.8) * mm, "end": v(-69.5, 110.2) * mm});
            skLineSegment(sketch, "E126.3.0.2", {"start": v(-70.5, -109.8) * mm, "end": v(-69.5, -109.8) * mm});
            skLineSegment(sketch, "E126.3.0.3", {"start": v(-69.5, 110.2) * mm, "end": v(-70.5, 110.2) * mm});
            skLineSegment(sketch, "E126.4.0.0", {"start": v(-60.5, 110.2) * mm, "end": v(-60.5, -109.8) * mm});
            skLineSegment(sketch, "E126.4.0.1", {"start": v(-59.5, -109.8) * mm, "end": v(-59.5, 110.2) * mm});
            skLineSegment(sketch, "E126.4.0.2", {"start": v(-60.5, -109.8) * mm, "end": v(-59.5, -109.8) * mm});
            skLineSegment(sketch, "E126.4.0.3", {"start": v(-59.5, 110.2) * mm, "end": v(-60.5, 110.2) * mm});
            skLineSegment(sketch, "E126.5.0.0", {"start": v(-50.5, 110.2) * mm, "end": v(-50.5, -109.8) * mm});
            skLineSegment(sketch, "E126.5.0.1", {"start": v(-49.5, -109.8) * mm, "end": v(-49.5, 110.2) * mm});
            skLineSegment(sketch, "E126.5.0.2", {"start": v(-50.5, -109.8) * mm, "end": v(-49.5, -109.8) * mm});
            skLineSegment(sketch, "E126.5.0.3", {"start": v(-49.5, 110.2) * mm, "end": v(-50.5, 110.2) * mm});
            skLineSegment(sketch, "E126.6.0.0", {"start": v(-40.5, 110.2) * mm, "end": v(-40.5, -109.8) * mm});
            skLineSegment(sketch, "E126.6.0.1", {"start": v(-39.5, -109.8) * mm, "end": v(-39.5, 110.2) * mm});
            skLineSegment(sketch, "E126.6.0.2", {"start": v(-40.5, -109.8) * mm, "end": v(-39.5, -109.8) * mm});
            skLineSegment(sketch, "E126.6.0.3", {"start": v(-39.5, 110.2) * mm, "end": v(-40.5, 110.2) * mm});
            skLineSegment(sketch, "E126.7.0.0", {"start": v(-30.5, 110.2) * mm, "end": v(-30.5, -109.8) * mm});
            skLineSegment(sketch, "E126.7.0.1", {"start": v(-29.5, -109.8) * mm, "end": v(-29.5, 110.2) * mm});
            skLineSegment(sketch, "E126.7.0.2", {"start": v(-30.5, -109.8) * mm, "end": v(-29.5, -109.8) * mm});
            skLineSegment(sketch, "E126.7.0.3", {"start": v(-29.5, 110.2) * mm, "end": v(-30.5, 110.2) * mm});
            skLineSegment(sketch, "E126.8.0.0", {"start": v(-20.5, 110.2) * mm, "end": v(-20.5, -109.8) * mm});
            skLineSegment(sketch, "E126.8.0.1", {"start": v(-19.5, -109.8) * mm, "end": v(-19.5, 110.2) * mm});
            skLineSegment(sketch, "E126.8.0.2", {"start": v(-20.5, -109.8) * mm, "end": v(-19.5, -109.8) * mm});
            skLineSegment(sketch, "E126.8.0.3", {"start": v(-19.5, 110.2) * mm, "end": v(-20.5, 110.2) * mm});
            skLineSegment(sketch, "E126.9.0.0", {"start": v(-10.5, 110.2) * mm, "end": v(-10.5, -109.8) * mm});
            skLineSegment(sketch, "E126.9.0.1", {"start": v(-9.5, -109.8) * mm, "end": v(-9.5, 110.2) * mm});
            skLineSegment(sketch, "E126.9.0.2", {"start": v(-10.5, -109.8) * mm, "end": v(-9.5, -109.8) * mm});
            skLineSegment(sketch, "E126.9.0.3", {"start": v(-9.5, 110.2) * mm, "end": v(-10.5, 110.2) * mm});
            skLineSegment(sketch, "E126.10.0.0", {"start": v(-0.5, 110.2) * mm, "end": v(-0.5, -109.8) * mm});
            skLineSegment(sketch, "E126.10.0.1", {"start": v(0.5, -109.8) * mm, "end": v(0.5, 110.2) * mm});
            skLineSegment(sketch, "E126.10.0.2", {"start": v(-0.5, -109.8) * mm, "end": v(0.5, -109.8) * mm});
            skLineSegment(sketch, "E126.10.0.3", {"start": v(0.5, 110.2) * mm, "end": v(-0.5, 110.2) * mm});
            skLineSegment(sketch, "E126.11.0.0", {"start": v(9.5, 110.2) * mm, "end": v(9.5, -109.8) * mm});
            skLineSegment(sketch, "E126.11.0.1", {"start": v(10.5, -109.8) * mm, "end": v(10.5, 110.2) * mm});
            skLineSegment(sketch, "E126.11.0.2", {"start": v(9.5, -109.8) * mm, "end": v(10.5, -109.8) * mm});
            skLineSegment(sketch, "E126.11.0.3", {"start": v(10.5, 110.2) * mm, "end": v(9.5, 110.2) * mm});
            skLineSegment(sketch, "E126.12.0.0", {"start": v(19.5, 110.2) * mm, "end": v(19.5, -109.8) * mm});
            skLineSegment(sketch, "E126.12.0.1", {"start": v(20.5, -109.8) * mm, "end": v(20.5, 110.2) * mm});
            skLineSegment(sketch, "E126.12.0.2", {"start": v(19.5, -109.8) * mm, "end": v(20.5, -109.8) * mm});
            skLineSegment(sketch, "E126.12.0.3", {"start": v(20.5, 110.2) * mm, "end": v(19.5, 110.2) * mm});
            skLineSegment(sketch, "E126.13.0.0", {"start": v(29.5, 110.2) * mm, "end": v(29.5, -109.8) * mm});
            skLineSegment(sketch, "E126.13.0.1", {"start": v(30.5, -109.8) * mm, "end": v(30.5, 110.2) * mm});
            skLineSegment(sketch, "E126.13.0.2", {"start": v(29.5, -109.8) * mm, "end": v(30.5, -109.8) * mm});
            skLineSegment(sketch, "E126.13.0.3", {"start": v(30.5, 110.2) * mm, "end": v(29.5, 110.2) * mm});
            skLineSegment(sketch, "E126.14.0.0", {"start": v(39.5, 110.2) * mm, "end": v(39.5, -109.8) * mm});
            skLineSegment(sketch, "E126.14.0.1", {"start": v(40.5, -109.8) * mm, "end": v(40.5, 110.2) * mm});
            skLineSegment(sketch, "E126.14.0.2", {"start": v(39.5, -109.8) * mm, "end": v(40.5, -109.8) * mm});
            skLineSegment(sketch, "E126.14.0.3", {"start": v(40.5, 110.2) * mm, "end": v(39.5, 110.2) * mm});
            skLineSegment(sketch, "E126.15.0.0", {"start": v(49.5, 110.2) * mm, "end": v(49.5, -109.8) * mm});
            skLineSegment(sketch, "E126.15.0.1", {"start": v(50.5, -109.8) * mm, "end": v(50.5, 110.2) * mm});
            skLineSegment(sketch, "E126.15.0.2", {"start": v(49.5, -109.8) * mm, "end": v(50.5, -109.8) * mm});
            skLineSegment(sketch, "E126.15.0.3", {"start": v(50.5, 110.2) * mm, "end": v(49.5, 110.2) * mm});
            skLineSegment(sketch, "E126.16.0.0", {"start": v(59.5, 110.2) * mm, "end": v(59.5, -109.8) * mm});
            skLineSegment(sketch, "E126.16.0.1", {"start": v(60.5, -109.8) * mm, "end": v(60.5, 110.2) * mm});
            skLineSegment(sketch, "E126.16.0.2", {"start": v(59.5, -109.8) * mm, "end": v(60.5, -109.8) * mm});
            skLineSegment(sketch, "E126.16.0.3", {"start": v(60.5, 110.2) * mm, "end": v(59.5, 110.2) * mm});
            skLineSegment(sketch, "E126.17.0.0", {"start": v(69.5, 110.2) * mm, "end": v(69.5, -109.8) * mm});
            skLineSegment(sketch, "E126.17.0.1", {"start": v(70.5, -109.8) * mm, "end": v(70.5, 110.2) * mm});
            skLineSegment(sketch, "E126.17.0.2", {"start": v(69.5, -109.8) * mm, "end": v(70.5, -109.8) * mm});
            skLineSegment(sketch, "E126.17.0.3", {"start": v(70.5, 110.2) * mm, "end": v(69.5, 110.2) * mm});
            skLineSegment(sketch, "E126.18.0.0", {"start": v(79.5, 110.2) * mm, "end": v(79.5, -109.8) * mm});
            skLineSegment(sketch, "E126.18.0.1", {"start": v(80.5, -109.8) * mm, "end": v(80.5, 110.2) * mm});
            skLineSegment(sketch, "E126.18.0.2", {"start": v(79.5, -109.8) * mm, "end": v(80.5, -109.8) * mm});
            skLineSegment(sketch, "E126.18.0.3", {"start": v(80.5, 110.2) * mm, "end": v(79.5, 110.2) * mm});
            skLineSegment(sketch, "E126.19.0.0", {"start": v(89.5, 110.2) * mm, "end": v(89.5, -109.8) * mm});
            skLineSegment(sketch, "E126.19.0.1", {"start": v(90.5, -109.8) * mm, "end": v(90.5, 110.2) * mm});
            skLineSegment(sketch, "E126.19.0.2", {"start": v(89.5, -109.8) * mm, "end": v(90.5, -109.8) * mm});
            skLineSegment(sketch, "E126.19.0.3", {"start": v(90.5, 110.2) * mm, "end": v(89.5, 110.2) * mm});
            skLineSegment(sketch, "E126.20.0.0", {"start": v(99.5, 110.2) * mm, "end": v(99.5, -109.8) * mm});
            skLineSegment(sketch, "E126.20.0.1", {"start": v(100.5, -109.8) * mm, "end": v(100.5, 110.2) * mm});
            skLineSegment(sketch, "E126.20.0.2", {"start": v(99.5, -109.8) * mm, "end": v(100.5, -109.8) * mm});
            skLineSegment(sketch, "E126.20.0.3", {"start": v(100.5, 110.2) * mm, "end": v(99.5, 110.2) * mm});
            skLineSegment(sketch, "E126.direction1", {"start": v(-100.5, -109.8) * mm, "end": v(-90.5, -109.8) * mm, "construction": true});
            skPoint(sketch, "E127", {"position": v(-100, 110.2) * mm});
            skPoint(sketch, "E128.0", {"position": v(-110, -109.8) * mm});
            skPoint(sketch, "E129.0", {"position": v(110, -109.8) * mm});
            skSolve(sketch);
        }
        {
            var Q0;
            Q0=makeQuery(id+"F6.imprint","IMPRINT",FACE,{"disambiguationData":[TD([[makeQuery(id+"F6.imprint","IMPRINT",EDGE,{"derivedFrom":sQuery(id+"F6.wireOp",EDGE,"E126.18.0.0")}),1.0]])]});
            var Q1;
            Q1=makeQuery(id+"F6.imprint","IMPRINT",FACE,{"disambiguationData":[TD([[makeQuery(id+"F6.imprint","IMPRINT",EDGE,{"derivedFrom":sQuery(id+"F6.wireOp",EDGE,"E126.17.0.0")}),1.0]])]});
            var Q2;
            Q2=makeQuery(id+"F6.imprint","IMPRINT",FACE,{"disambiguationData":[TD([[makeQuery(id+"F6.imprint","IMPRINT",EDGE,{"derivedFrom":sQuery(id+"F6.wireOp",EDGE,"E126.16.0.0")}),1.0]])]});
            var Q3;
            Q3=makeQuery(id+"F6.imprint","IMPRINT",FACE,{"disambiguationData":[TD([[makeQuery(id+"F6.imprint","IMPRINT",EDGE,{"derivedFrom":sQuery(id+"F6.wireOp",EDGE,"E126.9.0.0")}),1.0]])]});
            var Q4;
            Q4=makeQuery(id+"F6.imprint","IMPRINT",FACE,{"disambiguationData":[TD([[makeQuery(id+"F6.imprint","IMPRINT",EDGE,{"derivedFrom":sQuery(id+"F6.wireOp",EDGE,"E126.10.0.0")}),1.0]])]});
            var Q5;
            Q5=makeQuery(id+"F6.imprint","IMPRINT",FACE,{"disambiguationData":[TD([[makeQuery(id+"F6.imprint","IMPRINT",EDGE,{"derivedFrom":sQuery(id+"F6.wireOp",EDGE,"E126.11.0.0")}),1.0]])]});
            var Q6;
            Q6=makeQuery(id+"F6.imprint","IMPRINT",FACE,{"disambiguationData":[TD([[makeQuery(id+"F6.imprint","IMPRINT",EDGE,{"derivedFrom":sQuery(id+"F6.wireOp",EDGE,"E126.2.0.0")}),1.0]])]});
            var Q7;
            Q7=makeQuery(id+"F6.imprint","IMPRINT",FACE,{"disambiguationData":[TD([[makeQuery(id+"F6.imprint","IMPRINT",EDGE,{"derivedFrom":sQuery(id+"F6.wireOp",EDGE,"E126.3.0.0")}),1.0]])]});
            var Q8;
            Q8=makeQuery(id+"F6.imprint","IMPRINT",FACE,{"disambiguationData":[TD([[makeQuery(id+"F6.imprint","IMPRINT",EDGE,{"derivedFrom":sQuery(id+"F6.wireOp",EDGE,"E126.4.0.0")}),1.0]])]});
            var Q9;
            Q9=makeQuery(id+"F6.imprint","IMPRINT",FACE,{"disambiguationData":[TD([[makeQuery(id+"F6.imprint","IMPRINT",EDGE,{"derivedFrom":sQuery(id+"F6.wireOp",EDGE,"E122")}),1.0]])]});
            var Q10;
            Q10=makeQuery(id+"F6.imprint","IMPRINT",FACE,{"disambiguationData":[TD([[makeQuery(id+"F6.imprint","IMPRINT",EDGE,{"derivedFrom":sQuery(id+"F6.wireOp",EDGE,"E126.1.0.0")}),1.0]])]});
            var Q11;
            Q11=makeQuery(id+"F6.imprint","IMPRINT",FACE,{"disambiguationData":[TD([[makeQuery(id+"F6.imprint","IMPRINT",EDGE,{"derivedFrom":sQuery(id+"F6.wireOp",EDGE,"E126.5.0.0")}),1.0]])]});
            var Q12;
            Q12=makeQuery(id+"F6.imprint","IMPRINT",FACE,{"disambiguationData":[TD([[makeQuery(id+"F6.imprint","IMPRINT",EDGE,{"derivedFrom":sQuery(id+"F6.wireOp",EDGE,"E126.6.0.0")}),1.0]])]});
            var Q13;
            Q13=makeQuery(id+"F6.imprint","IMPRINT",FACE,{"disambiguationData":[TD([[makeQuery(id+"F6.imprint","IMPRINT",EDGE,{"derivedFrom":sQuery(id+"F6.wireOp",EDGE,"E126.7.0.0")}),1.0]])]});
            var Q14;
            Q14=makeQuery(id+"F6.imprint","IMPRINT",FACE,{"disambiguationData":[TD([[makeQuery(id+"F6.imprint","IMPRINT",EDGE,{"derivedFrom":sQuery(id+"F6.wireOp",EDGE,"E126.8.0.0")}),1.0]])]});
            var Q15;
            Q15=makeQuery(id+"F6.imprint","IMPRINT",FACE,{"disambiguationData":[TD([[makeQuery(id+"F6.imprint","IMPRINT",EDGE,{"derivedFrom":sQuery(id+"F6.wireOp",EDGE,"E126.12.0.0")}),1.0]])]});
            var Q16;
            Q16=makeQuery(id+"F6.imprint","IMPRINT",FACE,{"disambiguationData":[TD([[makeQuery(id+"F6.imprint","IMPRINT",EDGE,{"derivedFrom":sQuery(id+"F6.wireOp",EDGE,"E126.13.0.0")}),1.0]])]});
            var Q17;
            Q17=makeQuery(id+"F6.imprint","IMPRINT",FACE,{"disambiguationData":[TD([[makeQuery(id+"F6.imprint","IMPRINT",EDGE,{"derivedFrom":sQuery(id+"F6.wireOp",EDGE,"E126.14.0.0")}),1.0]])]});
            var Q18;
            Q18=makeQuery(id+"F6.imprint","IMPRINT",FACE,{"disambiguationData":[TD([[makeQuery(id+"F6.imprint","IMPRINT",EDGE,{"derivedFrom":sQuery(id+"F6.wireOp",EDGE,"E126.15.0.0")}),1.0]])]});
            var Q19;
            Q19=makeQuery(id+"F6.imprint","IMPRINT",FACE,{"disambiguationData":[TD([[makeQuery(id+"F6.imprint","IMPRINT",EDGE,{"derivedFrom":sQuery(id+"F6.wireOp",EDGE,"E126.19.0.0")}),1.0]])]});
            var Q20;
            Q20=makeQuery(id+"F6.imprint","IMPRINT",FACE,{"disambiguationData":[TD([[makeQuery(id+"F6.imprint","IMPRINT",EDGE,{"derivedFrom":sQuery(id+"F6.wireOp",EDGE,"E126.20.0.0")}),1.0]])]});
            extrude(context, id + "F7", {"entities" : qUnion([Q0, Q1, Q2, Q3, Q4, Q5, Q6, Q7, Q8, Q9, Q10, Q11, Q12, Q13, Q14, Q15, Q16, Q17, Q18, Q19, Q20]), "operationType" : NewBodyOperationType.ADD, "oppositeDirection" : true, "depth" : 5 * mm, "offsetDistance" : 25 * mm});
        }
        {
            var Q0;
            {var subQ0=sQuery(id+"F2.wireOp",EDGE,"E17.6");Q0=makeQuery(id+"F2.imprint","IMPRINT",FACE,{"disambiguationData":[TD([[makeQuery(id+"F2.imprint","IMPRINT",EDGE,{"derivedFrom":subQ0}),1.0]])]});}
            var Q1;
            {var subQ0=sQuery(id+"F2.wireOp",EDGE,"E17.4");Q1=makeQuery(id+"F2.imprint","IMPRINT",FACE,{"disambiguationData":[TD([[makeQuery(id+"F2.imprint","IMPRINT",EDGE,{"derivedFrom":subQ0}),1.0]])]});}
            var Q2;
            {var subQ5=sQuery(id+"F2.wireOp",EDGE,"E21");Q2=makeQuery(id+"F2.imprint","IMPRINT",FACE,{"disambiguationData":[TD([[makeQuery(id+"F2.imprint","IMPRINT",EDGE,{"derivedFrom":subQ5}),1.0]])]});}
            var Q3;
            {var subQ5=makeQuery(id+"F1.opExtrude","CAP_EDGE",EDGE,{"disambiguationData":[OSD([sQuery(id+"F0.wireOp",EDGE,"ffc58e78-ab67-4520-8160-0caf265e7499.bottom")])],"isStart":false});Q3=makeQuery(id+"F2.imprint","IMPRINT",FACE,{"disambiguationData":[TD([[makeQuery(id+"F2.imprint","IMPRINT",EDGE,{"derivedFrom":subQ5}),1.0]])]});}
            var Q4;
            {var subQ0=sQuery(id+"F2.wireOp",EDGE,"6c732197-0a9a-4348-96ec-b130dbe12e8a.6");Q4=makeQuery(id+"F2.imprint","IMPRINT",FACE,{"disambiguationData":[TD([[makeQuery(id+"F2.imprint","IMPRINT",EDGE,{"derivedFrom":subQ0}),1.0]])]});}
            var Q5;
            {var subQ0=sQuery(id+"F2.wireOp",EDGE,"987317ce-180a-4498-a472-00d99b00c620");Q5=makeQuery(id+"F2.imprint","IMPRINT",FACE,{"disambiguationData":[TD([[makeQuery(id+"F2.imprint","IMPRINT",EDGE,{"derivedFrom":subQ0}),1.0]])]});}
            var Q6;
            {var subQ5=makeQuery(id+"F1.opExtrude","CAP_EDGE",EDGE,{"disambiguationData":[OSD([sQuery(id+"F0.wireOp",EDGE,"b305908e-d21f-4fcc-82a1-d083eb46f08c.bottom")])],"isStart":false});Q6=makeQuery(id+"F2.imprint","IMPRINT",FACE,{"disambiguationData":[TD([[makeQuery(id+"F2.imprint","IMPRINT",EDGE,{"derivedFrom":subQ5}),1.0]])]});}
            var Q7;
            {var subQ0=sQuery(id+"F2.wireOp",EDGE,"6c732197-0a9a-4348-96ec-b130dbe12e8a.4");Q7=makeQuery(id+"F2.imprint","IMPRINT",FACE,{"disambiguationData":[TD([[makeQuery(id+"F2.imprint","IMPRINT",EDGE,{"derivedFrom":subQ0}),1.0]])]});}
            var Q8;
            {var subQ0=sQuery(id+"F2.wireOp",EDGE,"b7afeb6d-8188-4377-87fc-cda0c34afc78.4");Q8=makeQuery(id+"F2.imprint","IMPRINT",FACE,{"disambiguationData":[TD([[makeQuery(id+"F2.imprint","IMPRINT",EDGE,{"derivedFrom":subQ0}),1.0]])]});}
            var Q9;
            {var subQ0=sQuery(id+"F2.wireOp",EDGE,"7623e9e9-e2ef-4c7f-a875-663358ed1d73");Q9=makeQuery(id+"F2.imprint","IMPRINT",FACE,{"disambiguationData":[TD([[makeQuery(id+"F2.imprint","IMPRINT",EDGE,{"derivedFrom":subQ0}),-1.0]])]});}
            var Q10;
            {var subQ0=sQuery(id+"F2.wireOp",EDGE,"b7afeb6d-8188-4377-87fc-cda0c34afc78.5");var subQ1=makeQuery(id+"F1.opExtrude","CAP_EDGE",EDGE,{"disambiguationData":[OSD([sQuery(id+"F0.wireOp",EDGE,"050fb597-32a5-4862-9c33-4c7541ed5447.left")])],"isStart":false});var subQ2=makeQuery(id+"F2.imprint","INTERSECT",VERTEX,{"derivedFrom":[subQ1,subQ0]});Q10=makeQuery(id+"F2.imprint","IMPRINT",FACE,{"disambiguationData":[TD([[makeQuery(id+"F2.imprint","IMPRINT",EDGE,{"disambiguationData":[TD([[subQ2,-1.0]])],"derivedFrom":subQ0}),1.0]])]});}
            var Q11;
            {var subQ0=sQuery(id+"F2.wireOp",EDGE,"d5c14c10-3568-49e1-a069-6b8c7e1b838c");Q11=makeQuery(id+"F2.imprint","IMPRINT",FACE,{"disambiguationData":[TD([[makeQuery(id+"F2.imprint","IMPRINT",EDGE,{"derivedFrom":subQ0}),1.0]])]});}
            var Q12;
            {var subQ0=sQuery(id+"F2.wireOp",EDGE,"b7afeb6d-8188-4377-87fc-cda0c34afc78.6");Q12=makeQuery(id+"F2.imprint","IMPRINT",FACE,{"disambiguationData":[TD([[makeQuery(id+"F2.imprint","IMPRINT",EDGE,{"derivedFrom":subQ0}),1.0]])]});}
            var Q13;
            {var subQ0=sQuery(id+"F2.wireOp",EDGE,"376511b6-04c1-4115-bcfe-1b94a2ecceef.6");Q13=makeQuery(id+"F2.imprint","IMPRINT",FACE,{"disambiguationData":[TD([[makeQuery(id+"F2.imprint","IMPRINT",EDGE,{"derivedFrom":subQ0}),1.0]])]});}
            var Q14;
            {var subQ0=sQuery(id+"F2.wireOp",EDGE,"9fd8aef6-1447-498e-82c1-ad6d5ad8e72c");Q14=makeQuery(id+"F2.imprint","IMPRINT",FACE,{"disambiguationData":[TD([[makeQuery(id+"F2.imprint","IMPRINT",EDGE,{"derivedFrom":subQ0}),1.0]])]});}
            var Q15;
            {var subQ0=sQuery(id+"F2.wireOp",EDGE,"376511b6-04c1-4115-bcfe-1b94a2ecceef.5");var subQ1=makeQuery(id+"F1.opExtrude","CAP_EDGE",EDGE,{"disambiguationData":[OSD([sQuery(id+"F0.wireOp",EDGE,"796d922f-7def-4038-baac-653a5c7ec2cd.left")])],"isStart":false});var subQ2=makeQuery(id+"F2.imprint","INTERSECT",VERTEX,{"derivedFrom":[subQ1,subQ0]});Q15=makeQuery(id+"F2.imprint","IMPRINT",FACE,{"disambiguationData":[TD([[makeQuery(id+"F2.imprint","IMPRINT",EDGE,{"disambiguationData":[TD([[subQ2,-1.0]])],"derivedFrom":subQ0}),1.0]])]});}
            var Q16;
            {var subQ0=sQuery(id+"F2.wireOp",EDGE,"7d5b1d15-cdbd-4470-b544-500c7b49bf22");Q16=makeQuery(id+"F2.imprint","IMPRINT",FACE,{"disambiguationData":[TD([[makeQuery(id+"F2.imprint","IMPRINT",EDGE,{"derivedFrom":subQ0}),-1.0]])]});}
            var Q17;
            {var subQ0=sQuery(id+"F2.wireOp",EDGE,"376511b6-04c1-4115-bcfe-1b94a2ecceef.4");Q17=makeQuery(id+"F2.imprint","IMPRINT",FACE,{"disambiguationData":[TD([[makeQuery(id+"F2.imprint","IMPRINT",EDGE,{"derivedFrom":subQ0}),1.0]])]});}
            var Q18;
            {var subQ2=sQuery(id+"F2.wireOp",EDGE,"E29.MirrorCS");Q18=makeQuery(id+"F2.imprint","IMPRINT",FACE,{"disambiguationData":[TD([[makeQuery(id+"F2.imprint","IMPRINT",EDGE,{"derivedFrom":subQ2}),-1.0]])]});}
            var Q19;
            {var subQ0=sQuery(id+"F2.wireOp",EDGE,"E29.MirrorCS");Q19=makeQuery(id+"F2.imprint","IMPRINT",FACE,{"disambiguationData":[TD([[makeQuery(id+"F2.imprint","IMPRINT",EDGE,{"derivedFrom":subQ0}),1.0]])]});}
            var Q20;
            {var subQ0=sQuery(id+"F2.wireOp",EDGE,"E27.MirrorCS");Q20=makeQuery(id+"F2.imprint","IMPRINT",FACE,{"disambiguationData":[TD([[makeQuery(id+"F2.imprint","IMPRINT",EDGE,{"derivedFrom":subQ0}),-1.0]])]});}
            var Q21;
            {var subQ0=sQuery(id+"F2.wireOp",EDGE,"E36.MirrorCS");Q21=makeQuery(id+"F2.imprint","IMPRINT",FACE,{"disambiguationData":[TD([[makeQuery(id+"F2.imprint","IMPRINT",EDGE,{"derivedFrom":subQ0}),1.0]])]});}
            var Q22;
            {var subQ0=sQuery(id+"F2.wireOp",EDGE,"E36.MirrorCS");Q22=makeQuery(id+"F2.imprint","IMPRINT",FACE,{"disambiguationData":[TD([[makeQuery(id+"F2.imprint","IMPRINT",EDGE,{"derivedFrom":subQ0}),-1.0]])]});}
            var Q23;
            {var subQ0=sQuery(id+"F2.wireOp",EDGE,"E37.MirrorCS");Q23=makeQuery(id+"F2.imprint","IMPRINT",FACE,{"disambiguationData":[TD([[makeQuery(id+"F2.imprint","IMPRINT",EDGE,{"derivedFrom":subQ0}),1.0]])]});}
            var Q24;
            {var subQ0=sQuery(id+"F2.wireOp",EDGE,"E44.MirrorCS");Q24=makeQuery(id+"F2.imprint","IMPRINT",FACE,{"disambiguationData":[TD([[makeQuery(id+"F2.imprint","IMPRINT",EDGE,{"derivedFrom":subQ0}),-1.0]])]});}
            var Q25;
            {var subQ0=sQuery(id+"F2.wireOp",EDGE,"E39.MirrorCS");Q25=makeQuery(id+"F2.imprint","IMPRINT",FACE,{"disambiguationData":[TD([[makeQuery(id+"F2.imprint","IMPRINT",EDGE,{"derivedFrom":subQ0}),-1.0]])]});}
            var Q26;
            {var subQ0=sQuery(id+"F2.wireOp",EDGE,"E39.MirrorCS");Q26=makeQuery(id+"F2.imprint","IMPRINT",FACE,{"disambiguationData":[TD([[makeQuery(id+"F2.imprint","IMPRINT",EDGE,{"derivedFrom":subQ0}),1.0]])]});}
            extrude(context, id + "F8", {"entities" : qUnion([Q0, Q1, Q2, Q3, Q4, Q5, Q6, Q7, Q8, Q9, Q10, Q11, Q12, Q13, Q14, Q15, Q16, Q17, Q18, Q19, Q20, Q21, Q22, Q23, Q24, Q25, Q26]), "operationType" : NewBodyOperationType.REMOVE, "depth" : 25 * mm, "offsetDistance" : 25 * mm});
        }
        {
            var Q0;
            {var subQ5=sQuery(id+"F2.wireOp",EDGE,"E21");Q0=makeQuery(id+"F2.imprint","IMPRINT",FACE,{"disambiguationData":[TD([[makeQuery(id+"F2.imprint","IMPRINT",EDGE,{"derivedFrom":subQ5}),1.0]])]});}
            var Q1;
            {var subQ5=makeQuery(id+"F1.opExtrude","CAP_EDGE",EDGE,{"disambiguationData":[OSD([sQuery(id+"F0.wireOp",EDGE,"ffc58e78-ab67-4520-8160-0caf265e7499.bottom")])],"isStart":false});Q1=makeQuery(id+"F2.imprint","IMPRINT",FACE,{"disambiguationData":[TD([[makeQuery(id+"F2.imprint","IMPRINT",EDGE,{"derivedFrom":subQ5}),1.0]])]});}
            var Q2;
            {var subQ5=makeQuery(id+"F1.opExtrude","CAP_EDGE",EDGE,{"disambiguationData":[OSD([sQuery(id+"F0.wireOp",EDGE,"b305908e-d21f-4fcc-82a1-d083eb46f08c.bottom")])],"isStart":false});Q2=makeQuery(id+"F2.imprint","IMPRINT",FACE,{"disambiguationData":[TD([[makeQuery(id+"F2.imprint","IMPRINT",EDGE,{"derivedFrom":subQ5}),1.0]])]});}
            var Q3;
            {var subQ0=sQuery(id+"F2.wireOp",EDGE,"987317ce-180a-4498-a472-00d99b00c620");Q3=makeQuery(id+"F2.imprint","IMPRINT",FACE,{"disambiguationData":[TD([[makeQuery(id+"F2.imprint","IMPRINT",EDGE,{"derivedFrom":subQ0}),1.0]])]});}
            var Q4;
            {var subQ0=sQuery(id+"F2.wireOp",EDGE,"7623e9e9-e2ef-4c7f-a875-663358ed1d73");Q4=makeQuery(id+"F2.imprint","IMPRINT",FACE,{"disambiguationData":[TD([[makeQuery(id+"F2.imprint","IMPRINT",EDGE,{"derivedFrom":subQ0}),-1.0]])]});}
            var Q5;
            {var subQ0=sQuery(id+"F2.wireOp",EDGE,"b7afeb6d-8188-4377-87fc-cda0c34afc78.5");var subQ1=makeQuery(id+"F1.opExtrude","CAP_EDGE",EDGE,{"disambiguationData":[OSD([sQuery(id+"F0.wireOp",EDGE,"050fb597-32a5-4862-9c33-4c7541ed5447.left")])],"isStart":false});var subQ2=makeQuery(id+"F2.imprint","INTERSECT",VERTEX,{"derivedFrom":[subQ1,subQ0]});Q5=makeQuery(id+"F2.imprint","IMPRINT",FACE,{"disambiguationData":[TD([[makeQuery(id+"F2.imprint","IMPRINT",EDGE,{"disambiguationData":[TD([[subQ2,-1.0]])],"derivedFrom":subQ0}),1.0]])]});}
            var Q6;
            {var subQ0=sQuery(id+"F2.wireOp",EDGE,"d5c14c10-3568-49e1-a069-6b8c7e1b838c");Q6=makeQuery(id+"F2.imprint","IMPRINT",FACE,{"disambiguationData":[TD([[makeQuery(id+"F2.imprint","IMPRINT",EDGE,{"derivedFrom":subQ0}),1.0]])]});}
            var Q7;
            {var subQ0=sQuery(id+"F2.wireOp",EDGE,"7d5b1d15-cdbd-4470-b544-500c7b49bf22");Q7=makeQuery(id+"F2.imprint","IMPRINT",FACE,{"disambiguationData":[TD([[makeQuery(id+"F2.imprint","IMPRINT",EDGE,{"derivedFrom":subQ0}),-1.0]])]});}
            var Q8;
            {var subQ0=sQuery(id+"F2.wireOp",EDGE,"376511b6-04c1-4115-bcfe-1b94a2ecceef.5");var subQ1=makeQuery(id+"F1.opExtrude","CAP_EDGE",EDGE,{"disambiguationData":[OSD([sQuery(id+"F0.wireOp",EDGE,"796d922f-7def-4038-baac-653a5c7ec2cd.left")])],"isStart":false});var subQ2=makeQuery(id+"F2.imprint","INTERSECT",VERTEX,{"derivedFrom":[subQ1,subQ0]});Q8=makeQuery(id+"F2.imprint","IMPRINT",FACE,{"disambiguationData":[TD([[makeQuery(id+"F2.imprint","IMPRINT",EDGE,{"disambiguationData":[TD([[subQ2,-1.0]])],"derivedFrom":subQ0}),1.0]])]});}
            var Q9;
            {var subQ0=sQuery(id+"F2.wireOp",EDGE,"9fd8aef6-1447-498e-82c1-ad6d5ad8e72c");Q9=makeQuery(id+"F2.imprint","IMPRINT",FACE,{"disambiguationData":[TD([[makeQuery(id+"F2.imprint","IMPRINT",EDGE,{"derivedFrom":subQ0}),1.0]])]});}
            var Q10;
            {var subQ0=sQuery(id+"F2.wireOp",EDGE,"E29.MirrorCS");Q10=makeQuery(id+"F2.imprint","IMPRINT",FACE,{"disambiguationData":[TD([[makeQuery(id+"F2.imprint","IMPRINT",EDGE,{"derivedFrom":subQ0}),1.0]])]});}
            var Q11;
            {var subQ0=sQuery(id+"F2.wireOp",EDGE,"E36.MirrorCS");Q11=makeQuery(id+"F2.imprint","IMPRINT",FACE,{"disambiguationData":[TD([[makeQuery(id+"F2.imprint","IMPRINT",EDGE,{"derivedFrom":subQ0}),-1.0]])]});}
            var Q12;
            {var subQ0=sQuery(id+"F2.wireOp",EDGE,"E39.MirrorCS");Q12=makeQuery(id+"F2.imprint","IMPRINT",FACE,{"disambiguationData":[TD([[makeQuery(id+"F2.imprint","IMPRINT",EDGE,{"derivedFrom":subQ0}),-1.0]])]});}
            extrude(context, id + "F9", {"entities" : qUnion([Q0, Q1, Q2, Q3, Q4, Q5, Q6, Q7, Q8, Q9, Q10, Q11, Q12]), "operationType" : NewBodyOperationType.REMOVE, "oppositeDirection" : true, "depth" : 25 * mm, "offsetDistance" : 25 * mm});
        }
        {
            var Q0;
            Q0=qCreatedBy(makeId("Front.planeOp"),FACE);
            var sketch = newSketch(context, id + "F10", { "sketchPlane" : qUnion([Q0])});
            skCircle(sketch, "E130.1.0", {"center": v(64.8, 5.54) * mm, "radius": 4.5 * mm});
            skCircle(sketch, "E131", {"center": v(-64.8, 5.54) * mm, "radius": 4.5 * mm});
            skSolve(sketch);
        }
        {
            var Q0;
            Q0 = qSketchRegion(id + "F10", true);
            extrude(context, id + "F11", {"entities" : qUnion([Q0]), "operationType" : NewBodyOperationType.REMOVE, "oppositeDirection" : true, "depth" : 50 * mm, "offsetDistance" : 25 * mm, "symmetric" : true});
        }
    });
